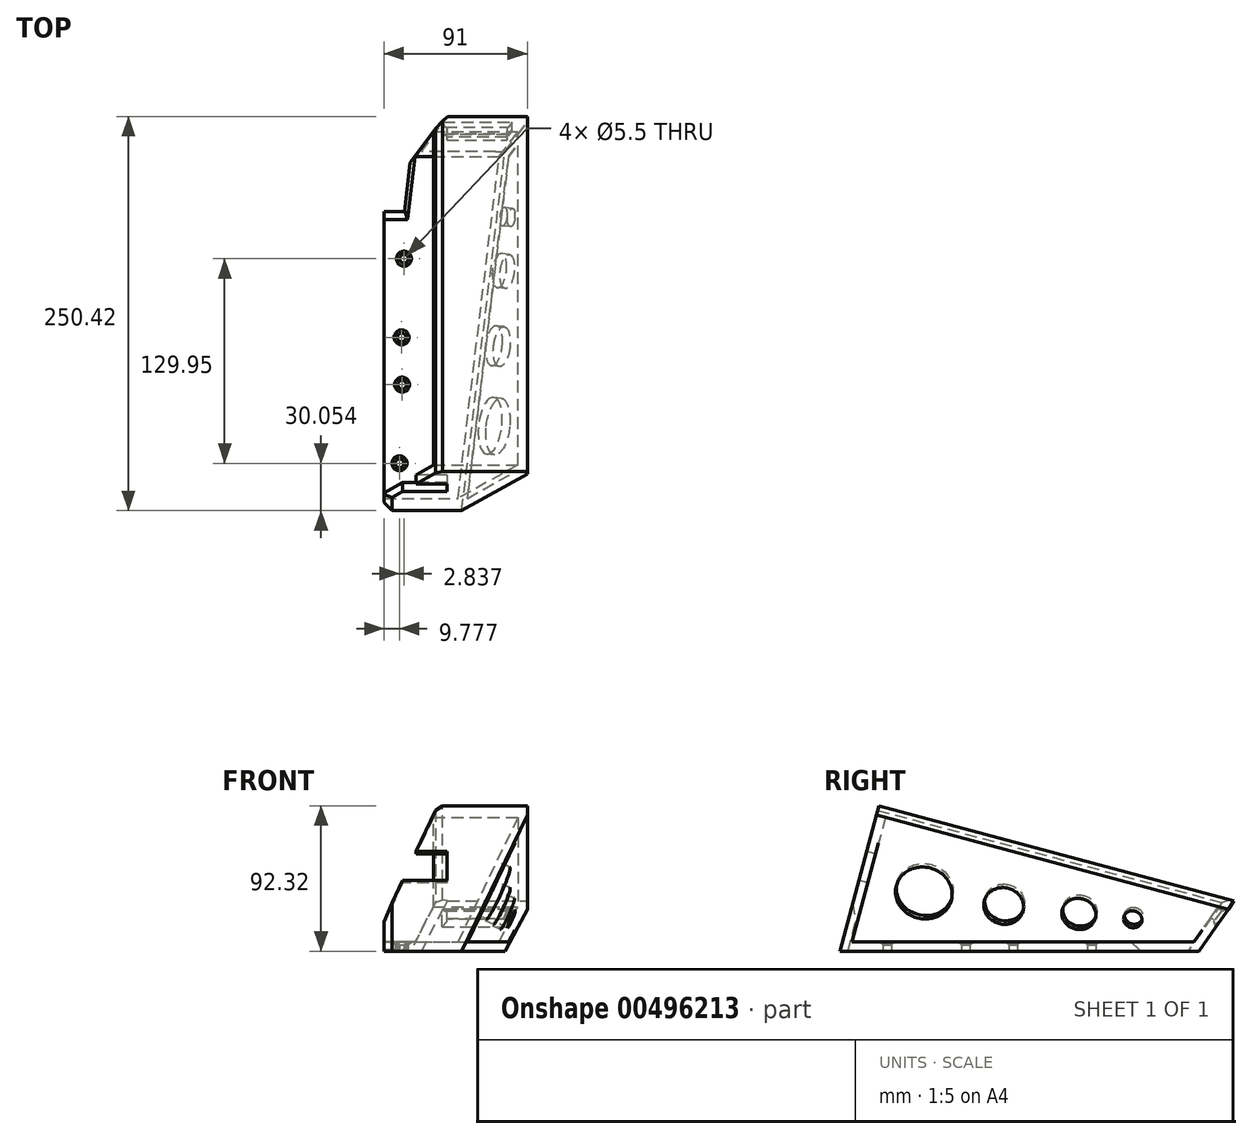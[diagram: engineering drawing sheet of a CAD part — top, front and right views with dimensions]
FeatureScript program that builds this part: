
annotation { "Feature Type Name" : "Feature", "Feature Type Description" : "" }
export const myFeature = defineFeature(function(context is Context, id is Id, definition is map)
    precondition{}
    {
        {
            var Q0;
            Q0=qCreatedBy(makeId("Right.planeOp"),FACE);
            var sketch = newSketch(context, id + "F0", { "sketchPlane" : qUnion([Q0])});
            skLineSegment(sketch, "E0", {"start": v(0, 0) * mm, "end": v(19.67, 73.41) * mm});
            skLineSegment(sketch, "E1", {"start": v(19.67, 73.41) * mm, "end": v(225.41, 18.28) * mm});
            skLineSegment(sketch, "E2", {"start": v(0, 0) * mm, "end": v(212.61, 0) * mm});
            skLineSegment(sketch, "E3", {"start": v(212.61, 0) * mm, "end": v(225.41, 18.28) * mm});
            skLineSegment(sketch, "E4.0", {"start": v(-3.26, -2.5) * mm, "end": v(17.9, 76.47) * mm});
            skLineSegment(sketch, "E4.1", {"start": v(-3.26, -2.5) * mm, "end": v(213.91, -2.5) * mm});
            skLineSegment(sketch, "E4.2", {"start": v(213.91, -2.5) * mm, "end": v(229.5, 19.77) * mm});
            skLineSegment(sketch, "E4.3", {"start": v(17.9, 76.47) * mm, "end": v(229.5, 19.77) * mm});
            skLineSegment(sketch, "E5.0", {"start": v(13.66, 83.82) * mm, "end": v(239.34, 23.35) * mm});
            skLineSegment(sketch, "E5.1", {"start": v(-11.08, -8.5) * mm, "end": v(13.66, 83.82) * mm});
            skLineSegment(sketch, "E5.2", {"start": v(-11.08, -8.5) * mm, "end": v(217.04, -8.5) * mm});
            skLineSegment(sketch, "E5.3", {"start": v(217.04, -8.5) * mm, "end": v(239.34, 23.35) * mm});
            skSolve(sketch);
        }
        {
            var Q0;
            Q0 = qSketchRegion(id + "F0", true);
            extrude(context, id + "F1", {"entities" : qUnion([Q0]), "oppositeDirection" : true, "depth" : 85 * mm});
        }
        {
            var Q0;
            Q0 = qSketchRegion(id + "F0", true);
            var Q1;
            Q1=makeQuery(id+"F0.imprint","IMPRINT",FACE,{"disambiguationData":[TD([[makeQuery(id+"F0.imprint","IMPRINT",EDGE,{"derivedFrom":sQuery(id+"F0.wireOp",EDGE,"E0")}),-1.0]])]});
            var Q2;
            Q2=makeQuery(id+"F0.imprint","IMPRINT",FACE,{"disambiguationData":[TD([[makeQuery(id+"F0.imprint","IMPRINT",EDGE,{"derivedFrom":sQuery(id+"F0.wireOp",EDGE,"E0")}),1.0]])]});
            extrude(context, id + "F2", {"entities" : qUnion([Q0, Q1, Q2]), "operationType" : NewBodyOperationType.ADD, "depth" : 6 * mm});
        }
        {
            var Q0;
            {var subQ0=sQuery(id+"F0.wireOp",EDGE,"E5.1");Q0=makeQuery(id+"F2.boolean.opBoolean","MERGE",FACE,{"derivedFrom":[makeQuery(id+"F1.opExtrude","SWEPT_FACE",FACE,{"disambiguationData":[OSD([subQ0])]}),makeQuery(id+"F2.opExtrude","SWEPT_FACE",FACE,{"disambiguationData":[OSD([subQ0])]})]});}
            var sketch = newSketch(context, id + "F3", { "sketchPlane" : qUnion([Q0])});
            skLineSegment(sketch, "E6.bottom", {"start": v(-85, 35.5) * mm, "end": v(-45, 35.5) * mm});
            skLineSegment(sketch, "E6.top", {"start": v(-85, 54.5) * mm, "end": v(-45, 54.5) * mm});
            skLineSegment(sketch, "E6.left", {"start": v(-85, 35.5) * mm, "end": v(-85, 54.5) * mm});
            skLineSegment(sketch, "E6.right", {"start": v(-45, 35.5) * mm, "end": v(-45, 54.5) * mm});
            skSolve(sketch);
        }
        {
            var Q0;
            Q0=makeQuery(id+"F3.imprint","IMPRINT",FACE,{"disambiguationData":[TD([[makeQuery(id+"F3.imprint","IMPRINT",EDGE,{"derivedFrom":sQuery(id+"F3.wireOp",EDGE,"E6.bottom")}),1.0]])]});
            extrude(context, id + "F4", {"entities" : qUnion([Q0]), "operationType" : NewBodyOperationType.REMOVE, "oppositeDirection" : true, "depth" : 25 * mm});
        }
        {
            var Q0;
            Q0=makeQuery(id+"F1.opExtrude","SWEPT_FACE",FACE,{"disambiguationData":[OSD([sQuery(id+"F0.wireOp",EDGE,"E4.0")])]});
            cPlane(context, id + "F5", {"entities" : qUnion([Q0]), "cplaneType" : CPlaneType.OFFSET, "offset" : 206.6 * mm, "width" : 150 * mm, "height" : 150 * mm});
        }
        {
            var Q0;
            Q0=qCreatedBy(id+"F5.planeOp",FACE);
            var sketch = newSketch(context, id + "F6", { "sketchPlane" : qUnion([Q0])});
            skLineSegment(sketch, "E7.bottom", {"start": v(6.9, 76.78) * mm, "end": v(45.18, 76.78) * mm});
            skLineSegment(sketch, "E7.top", {"start": v(6.9, 69.84) * mm, "end": v(45.18, 69.84) * mm});
            skLineSegment(sketch, "E7.left", {"start": v(6.9, 76.78) * mm, "end": v(6.9, 69.84) * mm});
            skLineSegment(sketch, "E7.right", {"start": v(45.18, 76.78) * mm, "end": v(45.18, 69.84) * mm});
            skSolve(sketch);
        }
        {
            var Q0;
            Q0=makeQuery(id+"F6.imprint","IMPRINT",FACE,{"disambiguationData":[TD([[makeQuery(id+"F6.imprint","IMPRINT",EDGE,{"derivedFrom":sQuery(id+"F6.wireOp",EDGE,"E7.bottom")}),-1.0]])]});
            extrude(context, id + "F7", {"entities" : qUnion([Q0]), "operationType" : NewBodyOperationType.REMOVE, "depth" : 35.7 * mm});
        }
        {
            var Q0;
            {var subQ0=sQuery(id+"F0.wireOp",EDGE,"E5.3");Q0=makeQuery(id+"F7.boolean.opBoolean","INTERSECT",EDGE,{"derivedFrom":[makeQuery(id+"F2.boolean.opBoolean","MERGE",FACE,{"derivedFrom":[makeQuery(id+"F1.opExtrude","SWEPT_FACE",FACE,{"disambiguationData":[OSD([subQ0])]}),makeQuery(id+"F2.opExtrude","SWEPT_FACE",FACE,{"disambiguationData":[OSD([subQ0])]})]}),makeQuery(id+"F7.opExtrude","SWEPT_FACE",FACE,{"disambiguationData":[OSD([sQuery(id+"F6.wireOp",EDGE,"E7.right")])]})]});}
            var Q1;
            {var subQ0=sQuery(id+"F0.wireOp",EDGE,"E5.3");Q1=makeQuery(id+"F7.boolean.opBoolean","INTERSECT",EDGE,{"derivedFrom":[makeQuery(id+"F2.boolean.opBoolean","MERGE",FACE,{"derivedFrom":[makeQuery(id+"F1.opExtrude","SWEPT_FACE",FACE,{"disambiguationData":[OSD([subQ0])]}),makeQuery(id+"F2.opExtrude","SWEPT_FACE",FACE,{"disambiguationData":[OSD([subQ0])]})]}),makeQuery(id+"F7.opExtrude","SWEPT_FACE",FACE,{"disambiguationData":[OSD([sQuery(id+"F6.wireOp",EDGE,"E7.bottom")])]})]});}
            var Q2;
            {var subQ0=sQuery(id+"F0.wireOp",EDGE,"E5.3");Q2=makeQuery(id+"F7.boolean.opBoolean","INTERSECT",EDGE,{"derivedFrom":[makeQuery(id+"F2.boolean.opBoolean","MERGE",FACE,{"derivedFrom":[makeQuery(id+"F1.opExtrude","SWEPT_FACE",FACE,{"disambiguationData":[OSD([subQ0])]}),makeQuery(id+"F2.opExtrude","SWEPT_FACE",FACE,{"disambiguationData":[OSD([subQ0])]})]}),makeQuery(id+"F7.opExtrude","SWEPT_FACE",FACE,{"disambiguationData":[OSD([sQuery(id+"F6.wireOp",EDGE,"E7.top")])]})]});}
            var Q3;
            {var subQ0=sQuery(id+"F0.wireOp",EDGE,"E5.3");Q3=makeQuery(id+"F7.boolean.opBoolean","INTERSECT",EDGE,{"derivedFrom":[makeQuery(id+"F2.boolean.opBoolean","MERGE",FACE,{"derivedFrom":[makeQuery(id+"F1.opExtrude","SWEPT_FACE",FACE,{"disambiguationData":[OSD([subQ0])]}),makeQuery(id+"F2.opExtrude","SWEPT_FACE",FACE,{"disambiguationData":[OSD([subQ0])]})]}),makeQuery(id+"F7.opExtrude","SWEPT_FACE",FACE,{"disambiguationData":[OSD([sQuery(id+"F6.wireOp",EDGE,"E7.left")])]})]});}
            chamfer(context, id + "F8", {"entities" : qUnion([Q0, Q1, Q2, Q3]), "width" : 3 * mm, "tangentPropagation" : true});
        }
        {
            var Q0;
            {var subQ0=sQuery(id+"F0.wireOp",EDGE,"E5.1");Q0=makeQuery(id+"F2.boolean.opBoolean","MERGE",FACE,{"derivedFrom":[makeQuery(id+"F1.opExtrude","SWEPT_FACE",FACE,{"disambiguationData":[OSD([subQ0])]}),makeQuery(id+"F2.opExtrude","SWEPT_FACE",FACE,{"disambiguationData":[OSD([subQ0])]})]});}
            var sketch = newSketch(context, id + "F9", { "sketchPlane" : qUnion([Q0])});
            skLineSegment(sketch, "E8", {"start": v(-85, 9.62) * mm, "end": v(-33.15, 123.76) * mm});
            skLineSegment(sketch, "E9", {"start": v(-33.15, 123.76) * mm, "end": v(-95.24, 117.13) * mm});
            skLineSegment(sketch, "E10", {"start": v(-95.24, 117.13) * mm, "end": v(-85, 9.62) * mm});
            skSolve(sketch);
        }
        {
            var Q0;
            Q0 = qSketchRegion(id + "F9", true);
            extrude(context, id + "F10", {"entities" : qUnion([Q0]), "operationType" : NewBodyOperationType.REMOVE, "oppositeDirection" : true, "depth" : 303 * mm});
        }
        {
            var Q0;
            Q0=makeQuery(id+"F1.opExtrude","CAP_FACE",FACE,{"disambiguationData":[OSD([sQuery(id+"F0.wireOp",EDGE,"E4.0"),sQuery(id+"F0.wireOp",EDGE,"E4.1"),sQuery(id+"F0.wireOp",EDGE,"E4.2"),sQuery(id+"F0.wireOp",EDGE,"E4.3"),sQuery(id+"F0.wireOp",EDGE,"E5.0"),sQuery(id+"F0.wireOp",EDGE,"E5.1"),sQuery(id+"F0.wireOp",EDGE,"E5.2"),sQuery(id+"F0.wireOp",EDGE,"E5.3")])],"isStart":false});
            var sketch = newSketch(context, id + "F11", { "sketchPlane" : qUnion([Q0])});
            skLineSegment(sketch, "E11.bottom", {"start": v(-28.92, -2.5) * mm, "end": v(-178.92, -2.5) * mm});
            skLineSegment(sketch, "E11.top", {"start": v(-28.92, -8.5) * mm, "end": v(-178.92, -8.5) * mm});
            skLineSegment(sketch, "E11.left", {"start": v(-28.92, -2.5) * mm, "end": v(-28.92, -8.5) * mm});
            skLineSegment(sketch, "E11.right", {"start": v(-178.92, -2.5) * mm, "end": v(-178.92, -8.5) * mm});
            skSolve(sketch);
        }
        {
            var Q0;
            {var subQ6=sQuery(id+"F11.wireOp",EDGE,"E11.right");Q0=makeQuery(id+"F11.imprint","IMPRINT",FACE,{"disambiguationData":[TD([[makeQuery(id+"F11.imprint","IMPRINT",EDGE,{"derivedFrom":subQ6}),1.0]])]});}
            var Q1;
            {var subQ6=sQuery(id+"F11.wireOp",EDGE,"E11.left");Q1=makeQuery(id+"F11.imprint","IMPRINT",FACE,{"disambiguationData":[TD([[makeQuery(id+"F11.imprint","IMPRINT",EDGE,{"derivedFrom":subQ6}),-1.0]])]});}
            extrude(context, id + "F12", {"entities" : qUnion([Q0, Q1]), "operationType" : NewBodyOperationType.ADD, "oppositeDirection" : true, "depth" : 34.2 * mm});
        }
        {
            var Q0;
            Q0=makeQuery(id+"F1.opExtrude","SWEPT_FACE",FACE,{"disambiguationData":[OSD([sQuery(id+"F0.wireOp",EDGE,"E4.0")])]});
            var sketch = newSketch(context, id + "F13", { "sketchPlane" : qUnion([Q0])});
            skLineSegment(sketch, "E12", {"start": v(0, 78.5) * mm, "end": v(38.12, -3.26) * mm});
            skLineSegment(sketch, "E13", {"start": v(38.12, -3.26) * mm, "end": v(32.13, -3.26) * mm});
            skLineSegment(sketch, "E14", {"start": v(32.13, -3.26) * mm, "end": v(-3.1, 72.26) * mm});
            skLineSegment(sketch, "E15", {"start": v(-3.1, 72.26) * mm, "end": v(0, 78.5) * mm});
            skSolve(sketch);
        }
        {
            var Q0;
            {var subQ0=sQuery(id+"F13.wireOp",EDGE,"E12");Q0=makeQuery(id+"F13.imprint","IMPRINT",FACE,{"disambiguationData":[TD([[makeQuery(id+"F13.imprint","IMPRINT",EDGE,{"derivedFrom":subQ0}),-1.0]])]});}
            extrude(context, id + "F14", {"entities" : qUnion([Q0]), "operationType" : NewBodyOperationType.ADD, "depth" : 241 * mm});
        }
        {
            var Q0;
            Q0=makeQuery(id+"F12.boolean.opBoolean","MERGE",FACE,{"derivedFrom":[makeQuery(id+"F1.opExtrude","CAP_FACE",FACE,{"disambiguationData":[OSD([sQuery(id+"F0.wireOp",EDGE,"E4.0"),sQuery(id+"F0.wireOp",EDGE,"E4.1"),sQuery(id+"F0.wireOp",EDGE,"E4.2"),sQuery(id+"F0.wireOp",EDGE,"E4.3"),sQuery(id+"F0.wireOp",EDGE,"E5.0"),sQuery(id+"F0.wireOp",EDGE,"E5.1"),sQuery(id+"F0.wireOp",EDGE,"E5.2"),sQuery(id+"F0.wireOp",EDGE,"E5.3")])],"isStart":false}),makeQuery(id+"F12.opExtrude","CAP_FACE",FACE,{"disambiguationData":[OSD([sQuery(id+"F11.wireOp",EDGE,"E11.bottom"),sQuery(id+"F11.wireOp",EDGE,"E11.top"),sQuery(id+"F11.wireOp",EDGE,"E11.left"),sQuery(id+"F11.wireOp",EDGE,"E11.right")])],"isStart":true})]});
            var sketch = newSketch(context, id + "F15", { "sketchPlane" : qUnion([Q0])});
            skLineSegment(sketch, "E16", {"start": v(11.08, -8.5) * mm, "end": v(-178.92, -8.5) * mm});
            skLineSegment(sketch, "E17", {"start": v(11.08, -8.5) * mm, "end": v(-217.04, -8.5) * mm});
            skLineSegment(sketch, "E18", {"start": v(-217.04, -8.5) * mm, "end": v(-239.34, 23.35) * mm});
            skLineSegment(sketch, "E19", {"start": v(-239.34, 23.35) * mm, "end": v(-265.95, 33.57) * mm});
            skLineSegment(sketch, "E20", {"start": v(-265.95, 33.57) * mm, "end": v(-270.5, -56.5) * mm});
            skLineSegment(sketch, "E21", {"start": v(-270.5, -56.5) * mm, "end": v(6.57, -76.53) * mm});
            skLineSegment(sketch, "E22", {"start": v(6.57, -76.53) * mm, "end": v(52.52, -24.2) * mm});
            skLineSegment(sketch, "E23", {"start": v(52.52, -24.2) * mm, "end": v(11.08, -8.5) * mm});
            skLineSegment(sketch, "E24", {"start": v(-270.5, -56.5) * mm, "end": v(-136.38, -152.37) * mm});
            skLineSegment(sketch, "E25", {"start": v(-136.38, -152.37) * mm, "end": v(6.57, -76.53) * mm});
            skSolve(sketch);
        }
        {
            var Q0;
            Q0 = qSketchRegion(id + "F15", true);
            extrude(context, id + "F16", {"entities" : qUnion([Q0]), "operationType" : NewBodyOperationType.REMOVE, "oppositeDirection" : true, "depth" : 197 * mm});
        }
        {
            var Q0;
            {var subQ0=sQuery(id+"F0.wireOp",EDGE,"E5.1");Q0=makeQuery(id+"F2.boolean.opBoolean","MERGE",FACE,{"derivedFrom":[makeQuery(id+"F1.opExtrude","SWEPT_FACE",FACE,{"disambiguationData":[OSD([subQ0])]}),makeQuery(id+"F2.opExtrude","SWEPT_FACE",FACE,{"disambiguationData":[OSD([subQ0])]})]});}
            var sketch = newSketch(context, id + "F17", { "sketchPlane" : qUnion([Q0])});
            skLineSegment(sketch, "E26", {"start": v(0, 65.65) * mm, "end": v(-14.59, 34.28) * mm});
            skLineSegment(sketch, "E27", {"start": v(-14.59, 34.28) * mm, "end": v(-37.28, -14.5) * mm});
            skLineSegment(sketch, "E28", {"start": v(-37.28, -14.5) * mm, "end": v(25.96, -16.7) * mm});
            skLineSegment(sketch, "E29", {"start": v(25.96, -16.7) * mm, "end": v(29.32, 80.38) * mm});
            skLineSegment(sketch, "E30", {"start": v(29.32, 80.38) * mm, "end": v(17.13, 108.11) * mm});
            skLineSegment(sketch, "E31", {"start": v(0, 65.65) * mm, "end": v(18.4, 105.21) * mm});
            skSolve(sketch);
        }
        {
            var Q0;
            {var subQ7=sQuery(id+"F17.wireOp",EDGE,"E26");Q0=makeQuery(id+"F17.imprint","IMPRINT",FACE,{"disambiguationData":[TD([[makeQuery(id+"F17.imprint","IMPRINT",EDGE,{"derivedFrom":subQ7}),1.0]])]});}
            extrude(context, id + "F18", {"entities" : qUnion([Q0]), "operationType" : NewBodyOperationType.REMOVE, "oppositeDirection" : true, "depth" : 1000 * mm});
        }
        {
            var Q0;
            {var subQ0=sQuery(id+"F0.wireOp",EDGE,"E5.0");Q0=makeQuery(id+"F10.boolean.opBoolean","INTERSECT",EDGE,{"derivedFrom":[makeQuery(id+"F2.boolean.opBoolean","MERGE",FACE,{"derivedFrom":[makeQuery(id+"F1.opExtrude","SWEPT_FACE",FACE,{"disambiguationData":[OSD([subQ0])]}),makeQuery(id+"F2.opExtrude","SWEPT_FACE",FACE,{"disambiguationData":[OSD([subQ0])]})]}),makeQuery(id+"F10.opExtrude","SWEPT_FACE",FACE,{"disambiguationData":[OSD([sQuery(id+"F9.wireOp",EDGE,"E8")])]})]});}
            chamfer(context, id + "F19", {"entities" : qUnion([Q0]), "width" : 5 * mm, "tangentPropagation" : true});
        }
        {
            var Q0;
            {var subQ0=sQuery(id+"F0.wireOp",EDGE,"E5.2");Q0=makeQuery(id+"F16.boolean.opBoolean","MERGE",FACE,{"derivedFrom":[makeQuery(id+"F12.boolean.opBoolean","MERGE",FACE,{"derivedFrom":[makeQuery(id+"F2.boolean.opBoolean","MERGE",FACE,{"derivedFrom":[makeQuery(id+"F1.opExtrude","SWEPT_FACE",FACE,{"disambiguationData":[OSD([subQ0])]}),makeQuery(id+"F2.opExtrude","SWEPT_FACE",FACE,{"disambiguationData":[OSD([subQ0])]})]}),makeQuery(id+"F12.opExtrude","SWEPT_FACE",FACE,{"disambiguationData":[OSD([sQuery(id+"F11.wireOp",EDGE,"E11.top")])]})]}),makeQuery(id+"F16.opExtrude","SWEPT_FACE",FACE,{"disambiguationData":[OSD([sQuery(id+"F15.wireOp",EDGE,"E17")])]})]});}
            var sketch = newSketch(context, id + "F20", { "sketchPlane" : qUnion([Q0])});
            skCircle(sketch, "E32", {"center": v(-73.9, -98.95) * mm, "radius": 2.75 * mm});
            skCircle(sketch, "E33", {"center": v(-72.39, -148.92) * mm, "radius": 2.75 * mm});
            skCircle(sketch, "E34", {"center": v(-73.58, -68.95) * mm, "radius": 2.75 * mm});
            skCircle(sketch, "E35", {"center": v(-75.22, -18.97) * mm, "radius": 2.75 * mm});
            skSolve(sketch);
        }
        {
            var Q0;
            Q0=makeQuery(id+"F20.imprint","IMPRINT",FACE,{"disambiguationData":[TD([[makeQuery(id+"F20.imprint","IMPRINT",EDGE,{"derivedFrom":sQuery(id+"F20.wireOp",EDGE,"E33")}),1.0]])]});
            var Q1;
            Q1=makeQuery(id+"F20.imprint","IMPRINT",FACE,{"disambiguationData":[TD([[makeQuery(id+"F20.imprint","IMPRINT",EDGE,{"derivedFrom":sQuery(id+"F20.wireOp",EDGE,"E32")}),1.0]])]});
            var Q2;
            Q2=makeQuery(id+"F20.imprint","IMPRINT",FACE,{"disambiguationData":[TD([[makeQuery(id+"F20.imprint","IMPRINT",EDGE,{"derivedFrom":sQuery(id+"F20.wireOp",EDGE,"E34")}),1.0]])]});
            var Q3;
            Q3=makeQuery(id+"F20.imprint","IMPRINT",FACE,{"disambiguationData":[TD([[makeQuery(id+"F20.imprint","IMPRINT",EDGE,{"derivedFrom":sQuery(id+"F20.wireOp",EDGE,"E35")}),1.0]])]});
            extrude(context, id + "F21", {"entities" : qUnion([Q0, Q1, Q2, Q3]), "operationType" : NewBodyOperationType.REMOVE, "oppositeDirection" : true, "depth" : 25 * mm});
        }
        {
            var Q0;
            Q0=makeQuery(id+"F14.boolean.opBoolean","SPLIT",FACE,{"disambiguationData":[TD([makeQuery(id+"F1.opExtrude","SWEPT_FACE",FACE,{"disambiguationData":[OSD([sQuery(id+"F0.wireOp",EDGE,"E4.0")])]})])],"derivedFrom":makeQuery(id+"F14.opExtrude","SWEPT_FACE",FACE,{"disambiguationData":[OSD([sQuery(id+"F13.wireOp",EDGE,"E12")])]})});
            var sketch = newSketch(context, id + "F22", { "sketchPlane" : qUnion([Q0])});
            skCircle(sketch, "E36", {"center": v(-39.5, 20.7) * mm, "radius": 18.1 * mm});
            skCircle(sketch, "E37", {"center": v(-90.54, 14.2) * mm, "radius": 12.77 * mm});
            skCircle(sketch, "E38", {"center": v(-138.58, 11) * mm, "radius": 10.89 * mm});
            skCircle(sketch, "E39", {"center": v(-173.04, 9) * mm, "radius": 5.88 * mm});
            skSolve(sketch);
        }
        {
            var Q0;
            Q0 = qSketchRegion(id + "F22", true);
            extrude(context, id + "F23", {"entities" : qUnion([Q0]), "operationType" : NewBodyOperationType.REMOVE, "oppositeDirection" : true, "depth" : 25 * mm});
        }
        {
            var Q0;
            Q0=makeQuery(id+"F12.opExtrude","SWEPT_EDGE",EDGE,{"disambiguationData":[OSD([sQuery(id+"F11.wireOp",EDGE,"E11.bottom"),sQuery(id+"F11.wireOp",EDGE,"E11.right")])]});
            var Q1;
            {var subQ0=sQuery(id+"F0.wireOp",EDGE,"E5.3");Q1=makeQuery(id+"F10.boolean.opBoolean","INTERSECT",EDGE,{"derivedFrom":[makeQuery(id+"F2.boolean.opBoolean","MERGE",FACE,{"derivedFrom":[makeQuery(id+"F1.opExtrude","SWEPT_FACE",FACE,{"disambiguationData":[OSD([subQ0])]}),makeQuery(id+"F2.opExtrude","SWEPT_FACE",FACE,{"disambiguationData":[OSD([subQ0])]})]}),makeQuery(id+"F10.opExtrude","SWEPT_FACE",FACE,{"disambiguationData":[OSD([sQuery(id+"F9.wireOp",EDGE,"E8")])]})]});}
            var Q2;
            {var subQ1=sQuery(id+"F0.wireOp",EDGE,"E5.0");var subQ2=sQuery(id+"F9.wireOp",EDGE,"E8");Q2=makeQuery(id+"F10.boolean.opBoolean","COPY",EDGE,{"disambiguationData":[TD([makeQuery(id+"F1.opExtrude","SWEPT_FACE",FACE,{"disambiguationData":[OSD([subQ1])]})])],"derivedFrom":makeQuery(id+"F10.opExtrude","CAP_EDGE",EDGE,{"disambiguationData":[OSD([subQ2])],"isStart":true})});}
            var Q3;
            {var subQ1=sQuery(id+"F9.wireOp",EDGE,"E8");Q3=makeQuery(id+"F10.boolean.opBoolean","COPY",EDGE,{"disambiguationData":[TD([makeQuery(id+"F4.boolean.opBoolean","COPY",FACE,{"derivedFrom":makeQuery(id+"F4.opExtrude","SWEPT_FACE",FACE,{"disambiguationData":[OSD([sQuery(id+"F3.wireOp",EDGE,"E6.bottom")])]})})])],"derivedFrom":makeQuery(id+"F10.opExtrude","CAP_EDGE",EDGE,{"disambiguationData":[OSD([subQ1])],"isStart":true})});}
            var Q4;
            {var subQ0=sQuery(id+"F0.wireOp",EDGE,"E5.1");var subQ1=sQuery(id+"F0.wireOp",EDGE,"E5.2");Q4=makeQuery(id+"F4.boolean.opBoolean","SPLIT",EDGE,{"disambiguationData":[TD([makeQuery(id+"F1.opExtrude","SWEPT_FACE",FACE,{"disambiguationData":[OSD([subQ1])]})])],"derivedFrom":makeQuery(id+"F1.opExtrude","CAP_EDGE",EDGE,{"disambiguationData":[OSD([subQ0])],"isStart":false})});}
            chamfer(context, id + "F24", {"entities" : qUnion([Q0, Q1, Q2, Q3, Q4]), "width" : 5 * mm, "tangentPropagation" : true});
        }
        {
            var Q0;
            {var subQ7=sQuery(id+"F0.wireOp",EDGE,"E4.1");var subQ11=makeQuery(id+"F1.opExtrude","SWEPT_FACE",FACE,{"disambiguationData":[OSD([subQ7])]});var subQ12=sQuery(id+"F11.wireOp",EDGE,"E11.right");var subQ13=sQuery(id+"F11.wireOp",EDGE,"E11.bottom");Q0=makeQuery(id+"F21.boolean.opBoolean","INTERSECT",EDGE,{"derivedFrom":[makeQuery(id+"F14.boolean.opBoolean","SPLIT",FACE,{"disambiguationData":[TD([makeQuery(id+"F12.opExtrude","SWEPT_FACE",FACE,{"disambiguationData":[OSD([subQ12])]})])],"derivedFrom":makeQuery(id+"F12.boolean.opBoolean","MERGE",FACE,{"derivedFrom":[subQ11,makeQuery(id+"F12.opExtrude","SWEPT_FACE",FACE,{"disambiguationData":[OSD([subQ13])]})]})}),makeQuery(id+"F21.opExtrude","SWEPT_FACE",FACE,{"disambiguationData":[OSD([sQuery(id+"F20.wireOp",EDGE,"E33")])]})]});}
            var Q1;
            {var subQ7=sQuery(id+"F0.wireOp",EDGE,"E4.1");var subQ11=makeQuery(id+"F1.opExtrude","SWEPT_FACE",FACE,{"disambiguationData":[OSD([subQ7])]});var subQ12=sQuery(id+"F11.wireOp",EDGE,"E11.right");var subQ13=sQuery(id+"F11.wireOp",EDGE,"E11.bottom");Q1=makeQuery(id+"F21.boolean.opBoolean","INTERSECT",EDGE,{"derivedFrom":[makeQuery(id+"F14.boolean.opBoolean","SPLIT",FACE,{"disambiguationData":[TD([makeQuery(id+"F12.opExtrude","SWEPT_FACE",FACE,{"disambiguationData":[OSD([subQ12])]})])],"derivedFrom":makeQuery(id+"F12.boolean.opBoolean","MERGE",FACE,{"derivedFrom":[subQ11,makeQuery(id+"F12.opExtrude","SWEPT_FACE",FACE,{"disambiguationData":[OSD([subQ13])]})]})}),makeQuery(id+"F21.opExtrude","SWEPT_FACE",FACE,{"disambiguationData":[OSD([sQuery(id+"F20.wireOp",EDGE,"E32")])]})]});}
            var Q2;
            {var subQ7=sQuery(id+"F0.wireOp",EDGE,"E4.1");var subQ11=makeQuery(id+"F1.opExtrude","SWEPT_FACE",FACE,{"disambiguationData":[OSD([subQ7])]});var subQ12=sQuery(id+"F11.wireOp",EDGE,"E11.right");var subQ13=sQuery(id+"F11.wireOp",EDGE,"E11.bottom");Q2=makeQuery(id+"F21.boolean.opBoolean","INTERSECT",EDGE,{"derivedFrom":[makeQuery(id+"F14.boolean.opBoolean","SPLIT",FACE,{"disambiguationData":[TD([makeQuery(id+"F12.opExtrude","SWEPT_FACE",FACE,{"disambiguationData":[OSD([subQ12])]})])],"derivedFrom":makeQuery(id+"F12.boolean.opBoolean","MERGE",FACE,{"derivedFrom":[subQ11,makeQuery(id+"F12.opExtrude","SWEPT_FACE",FACE,{"disambiguationData":[OSD([subQ13])]})]})}),makeQuery(id+"F21.opExtrude","SWEPT_FACE",FACE,{"disambiguationData":[OSD([sQuery(id+"F20.wireOp",EDGE,"E34")])]})]});}
            var Q3;
            {var subQ7=sQuery(id+"F0.wireOp",EDGE,"E4.1");var subQ11=makeQuery(id+"F1.opExtrude","SWEPT_FACE",FACE,{"disambiguationData":[OSD([subQ7])]});var subQ12=sQuery(id+"F11.wireOp",EDGE,"E11.right");var subQ13=sQuery(id+"F11.wireOp",EDGE,"E11.bottom");Q3=makeQuery(id+"F21.boolean.opBoolean","INTERSECT",EDGE,{"derivedFrom":[makeQuery(id+"F14.boolean.opBoolean","SPLIT",FACE,{"disambiguationData":[TD([makeQuery(id+"F12.opExtrude","SWEPT_FACE",FACE,{"disambiguationData":[OSD([subQ12])]})])],"derivedFrom":makeQuery(id+"F12.boolean.opBoolean","MERGE",FACE,{"derivedFrom":[subQ11,makeQuery(id+"F12.opExtrude","SWEPT_FACE",FACE,{"disambiguationData":[OSD([subQ13])]})]})}),makeQuery(id+"F21.opExtrude","SWEPT_FACE",FACE,{"disambiguationData":[OSD([sQuery(id+"F20.wireOp",EDGE,"E35")])]})]});}
            chamfer(context, id + "F25", {"entities" : qUnion([Q0, Q1, Q2, Q3]), "width" : 2 * mm, "tangentPropagation" : true});
        }
    });
